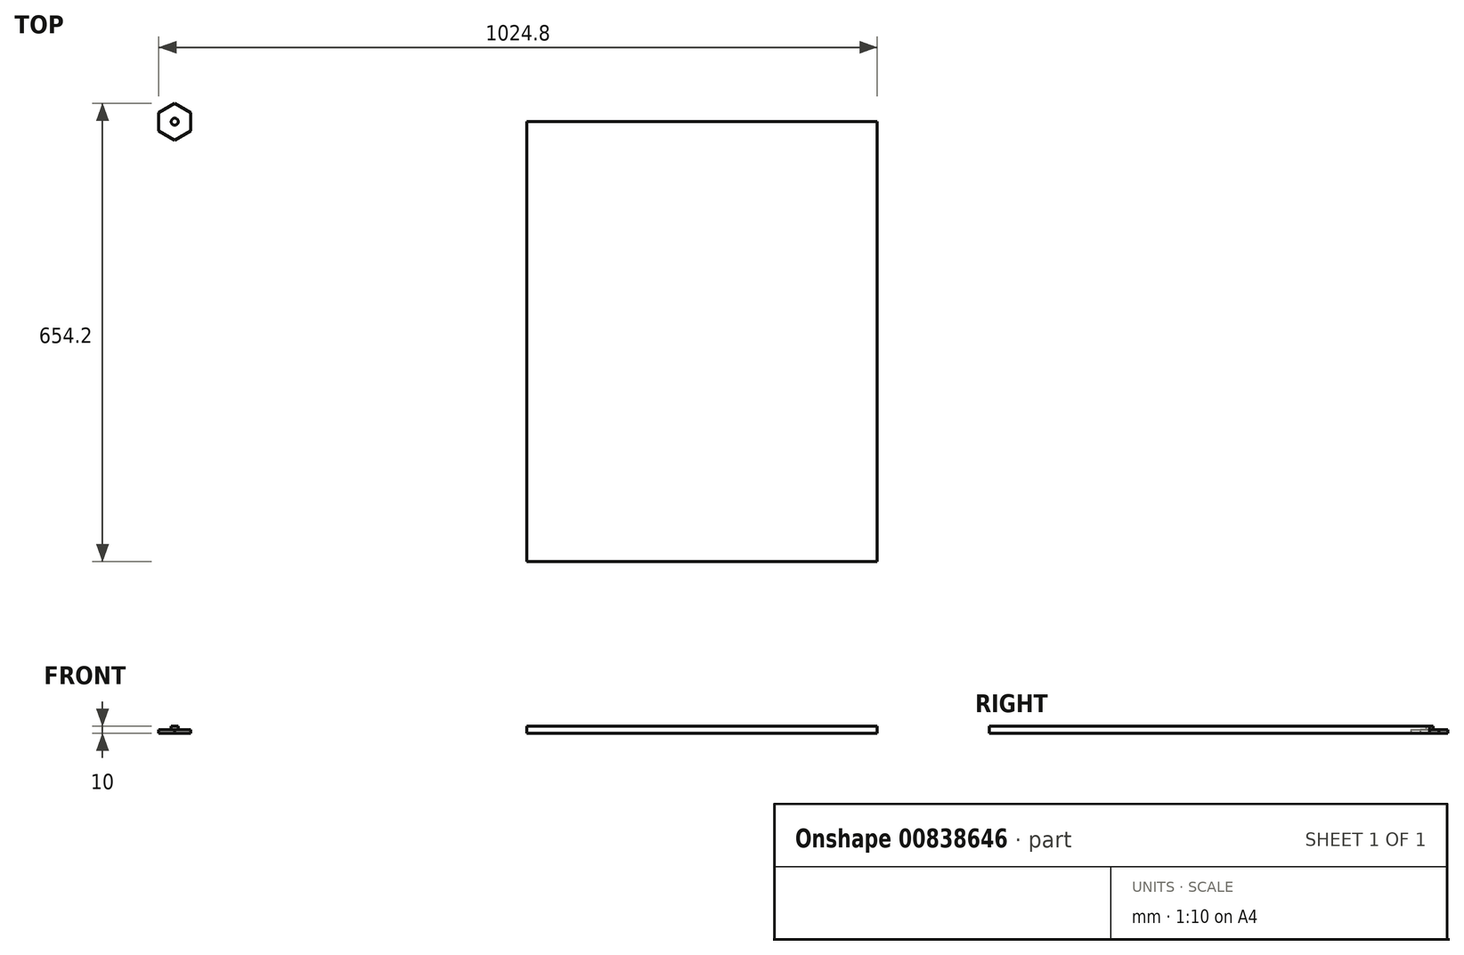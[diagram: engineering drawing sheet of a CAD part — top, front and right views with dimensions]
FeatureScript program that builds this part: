
annotation { "Feature Type Name" : "Feature", "Feature Type Description" : "" }
export const myFeature = defineFeature(function(context is Context, id is Id, definition is map)
    precondition{}
    {
        {
            var Q0;
            Q0=qCreatedBy(makeId("Top.planeOp"),FACE);
            var sketch = newSketch(context, id + "F0", { "sketchPlane" : qUnion([Q0])});
            skCircle(sketch, "E0.cCircle", {"center": v(0, 0) * mm, "radius": 22.8 * mm, "construction": true});
            skLineSegment(sketch, "E0.0", {"start": v(22.8, 13.16) * mm, "end": v(22.8, -13.16) * mm});
            skLineSegment(sketch, "E0.1", {"start": v(22.8, -13.16) * mm, "end": v(0, -26.32) * mm});
            skLineSegment(sketch, "E0.2", {"start": v(0, -26.32) * mm, "end": v(-22.8, -13.16) * mm});
            skLineSegment(sketch, "E0.3", {"start": v(-22.8, -13.16) * mm, "end": v(-22.8, 13.16) * mm});
            skLineSegment(sketch, "E0.4", {"start": v(-22.8, 13.16) * mm, "end": v(0, 26.32) * mm});
            skLineSegment(sketch, "E0.5", {"start": v(0, 26.32) * mm, "end": v(22.8, 13.16) * mm});
            skPoint(sketch, "E0.0.midPoint", {"position": v(22.8, 0) * mm});
            skSolve(sketch);
        }
        {
            var Q0;
            Q0 = qSketchRegion(id + "F0", true);
            extrude(context, id + "F1", {"entities" : qUnion([Q0]), "depth" : 5 * mm, "offsetDistance" : 25 * mm});
        }
        {
            var Q0;
            Q0=makeQuery(id+"F1.opExtrude","CAP_FACE",FACE,{"disambiguationData":[OSD([sQuery(id+"F0.wireOp",EDGE,"E0.0"),sQuery(id+"F0.wireOp",EDGE,"E0.1"),sQuery(id+"F0.wireOp",EDGE,"E0.2"),sQuery(id+"F0.wireOp",EDGE,"E0.3"),sQuery(id+"F0.wireOp",EDGE,"E0.4"),sQuery(id+"F0.wireOp",EDGE,"E0.5")])],"isStart":false});
            var sketch = newSketch(context, id + "F2", { "sketchPlane" : qUnion([Q0])});
            skCircle(sketch, "E1", {"center": v(0, 0) * mm, "radius": 5 * mm});
            skSolve(sketch);
        }
        {
            var Q0;
            Q0 = qSketchRegion(id + "F2", true);
            extrude(context, id + "F3", {"entities" : qUnion([Q0]), "operationType" : NewBodyOperationType.ADD, "depth" : 5 * mm, "offsetDistance" : 25 * mm});
        }
        {
            var Q0;
            Q0=qCreatedBy(makeId("Top.planeOp"),FACE);
            var sketch = newSketch(context, id + "F4", { "sketchPlane" : qUnion([Q0])});
            skLineSegment(sketch, "E2.bottom", {"start": v(502, 0) * mm, "end": v(1002, 0) * mm});
            skLineSegment(sketch, "E2.top", {"start": v(502, -627.88) * mm, "end": v(1002, -627.88) * mm});
            skLineSegment(sketch, "E2.left", {"start": v(502, 0) * mm, "end": v(502, -627.88) * mm});
            skLineSegment(sketch, "E2.right", {"start": v(1002, 0) * mm, "end": v(1002, -627.88) * mm});
            skSolve(sketch);
        }
        {
            var Q0;
            Q0=makeQuery(id+"F4.imprint","IMPRINT",FACE,{"disambiguationData":[TD([[makeQuery(id+"F4.imprint","IMPRINT",EDGE,{"derivedFrom":sQuery(id+"F4.wireOp",EDGE,"E2.bottom")}),-1.0]])]});
            extrude(context, id + "F5", {"entities" : qUnion([Q0]), "depth" : 10 * mm, "offsetDistance" : 25 * mm});
        }
    });
